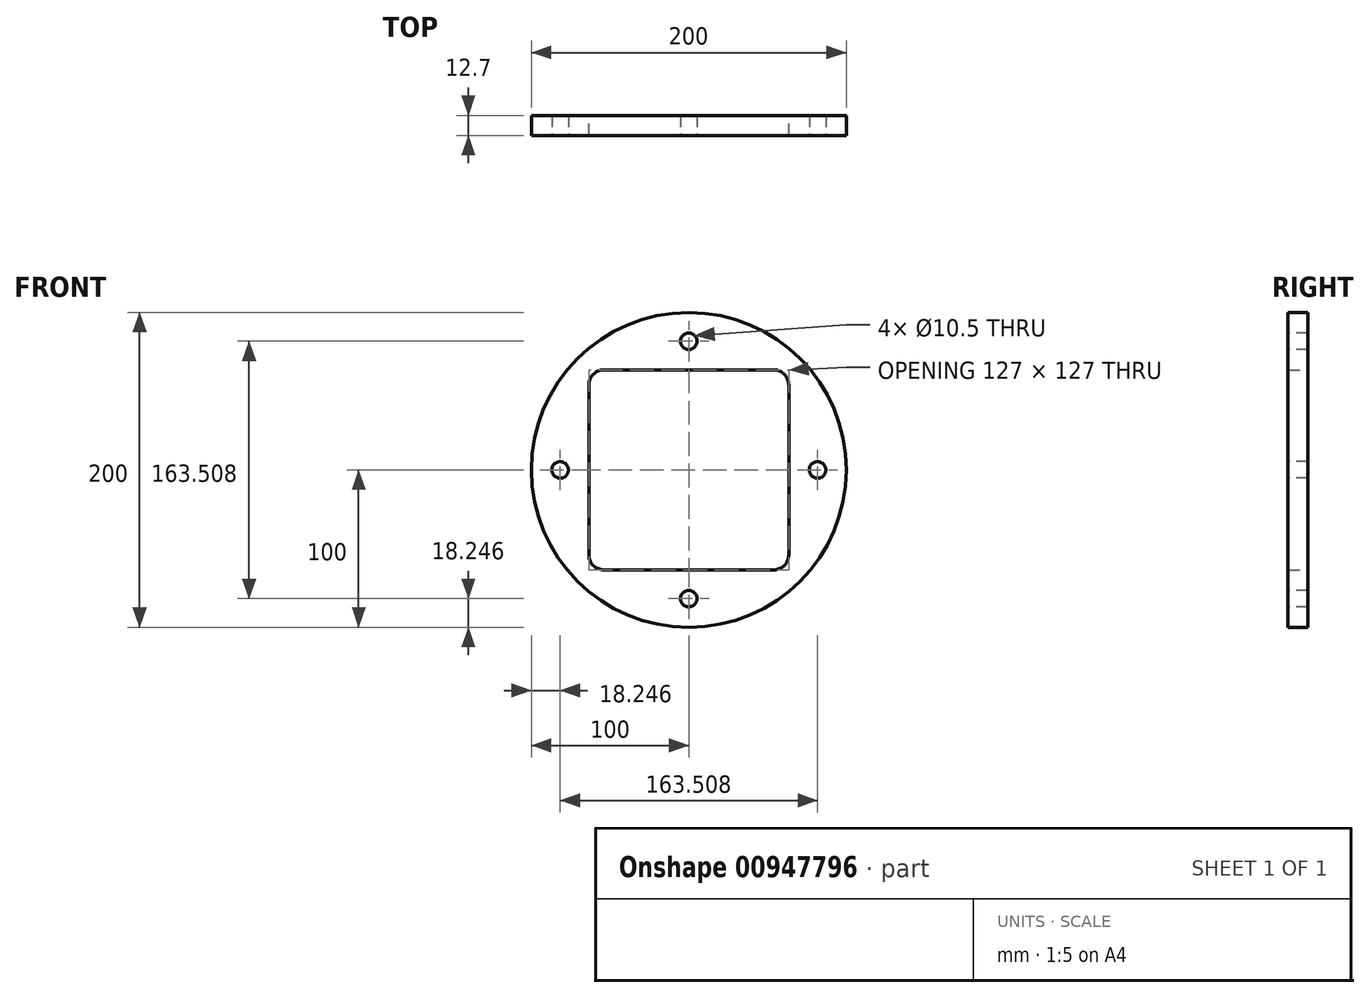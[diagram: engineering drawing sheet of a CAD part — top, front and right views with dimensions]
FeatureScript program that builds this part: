
annotation { "Feature Type Name" : "Feature", "Feature Type Description" : "" }
export const myFeature = defineFeature(function(context is Context, id is Id, definition is map)
    precondition{}
    {
        {
            var Q0;
            Q0=qCreatedBy(makeId("Front.planeOp"),FACE);
            var sketch = newSketch(context, id + "F0", { "sketchPlane" : qUnion([Q0])});
            skCircle(sketch, "E0", {"center": v(0, 0) * mm, "radius": 100 * mm});
            skLineSegment(sketch, "E1.bottom", {"start": v(53.95, -63.5) * mm, "end": v(-53.95, -63.5) * mm});
            skLineSegment(sketch, "E1.top", {"start": v(53.95, 63.5) * mm, "end": v(-53.95, 63.5) * mm});
            skLineSegment(sketch, "E1.left", {"start": v(63.5, -53.95) * mm, "end": v(63.5, 53.95) * mm});
            skLineSegment(sketch, "E1.right", {"start": v(-63.5, -53.95) * mm, "end": v(-63.5, 53.95) * mm});
            skPoint(sketch, "E2.visualSharp", {"position": v(-63.5, 63.5) * mm});
            skArc(sketch, "E2.filletArc", {"start": v(-53.95, 63.5) * mm, "mid": v(-60.7, 60.7) * mm, "end": v(-63.5, 53.95) * mm});
            skPoint(sketch, "E3.visualSharp", {"position": v(63.5, 63.5) * mm});
            skArc(sketch, "E3.filletArc", {"start": v(63.5, 53.95) * mm, "mid": v(60.7, 60.7) * mm, "end": v(53.95, 63.5) * mm});
            skPoint(sketch, "E4.visualSharp", {"position": v(63.5, -63.5) * mm});
            skArc(sketch, "E4.filletArc", {"start": v(53.95, -63.5) * mm, "mid": v(60.7, -60.7) * mm, "end": v(63.5, -53.95) * mm});
            skPoint(sketch, "E5.visualSharp", {"position": v(-63.5, -63.5) * mm});
            skArc(sketch, "E5.filletArc", {"start": v(-63.5, -53.95) * mm, "mid": v(-60.7, -60.7) * mm, "end": v(-53.95, -63.5) * mm});
            skPoint(sketch, "E6", {"position": v(0, 81.75) * mm});
            skPoint(sketch, "E7.1.0", {"position": v(-81.75, 0) * mm});
            skPoint(sketch, "E7.2.0", {"position": v(0, -81.75) * mm});
            skPoint(sketch, "E7.3.0", {"position": v(81.75, 0) * mm});
            skSolve(sketch);
        }
        {
            var Q0;
            Q0 = qSketchRegion(id + "F0", true);
            extrude(context, id + "F1", {"entities" : qUnion([Q0]), "depth" : 12.7 * mm, "offsetDistance" : 25 * mm});
        }
        {
            var Q0;
            Q0=sQuery(id+"F0.wireOp",VERTEX,"E6");
            var Q1;
            Q1=sQuery(id+"F0.wireOp",VERTEX,"E7.3.0");
            var Q2;
            Q2=sQuery(id+"F0.wireOp",VERTEX,"E7.2.0");
            var Q3;
            Q3=sQuery(id+"F0.wireOp",VERTEX,"E7.1.0");
            var Q4;
            Q4=makeQuery(id+"F1.opExtrude","SWEPT_BODY",BODY,{"disambiguationData":[OSD([sQuery(id+"F0.wireOp",EDGE,"E0"),sQuery(id+"F0.wireOp",EDGE,"E1.bottom"),sQuery(id+"F0.wireOp",EDGE,"E1.top"),sQuery(id+"F0.wireOp",EDGE,"E1.left"),sQuery(id+"F0.wireOp",EDGE,"E1.right"),sQuery(id+"F0.wireOp",EDGE,"E2.filletArc"),sQuery(id+"F0.wireOp",EDGE,"E3.filletArc"),sQuery(id+"F0.wireOp",EDGE,"E4.filletArc"),sQuery(id+"F0.wireOp",EDGE,"E5.filletArc")])]});
            hole(context, id + "F2", {"style" : HoleStyle.SIMPLE, "endStyle" : HoleEndStyle.THROUGH, "oppositeDirection" : true, "standardTappedOrClearance" : lookupTablePath({ "fit" : "Close", "standard" : "ISO", "size" : "M10", "type" : "Clearance" }), "standardBlindInLast" : lookupTablePath({ "fit" : "Close", "standard" : "ISO", "engagement" : "75%", "pitch" : "1.5 mm", "size" : "M10", "type" : "Clearance & tapped" }), "holeDiameter" : 10.5 * mm, "majorDiameter" : 5 * mm, "isTappedThrough" : true, "tappedDepth" : 40.45 * mm, "tapClearance" : 3, "locations" : qUnion([Q0, Q1, Q2, Q3]), "scope" : qUnion([Q4]), "startStyle" : HoleStartStyle.SKETCH});
        }
    });
